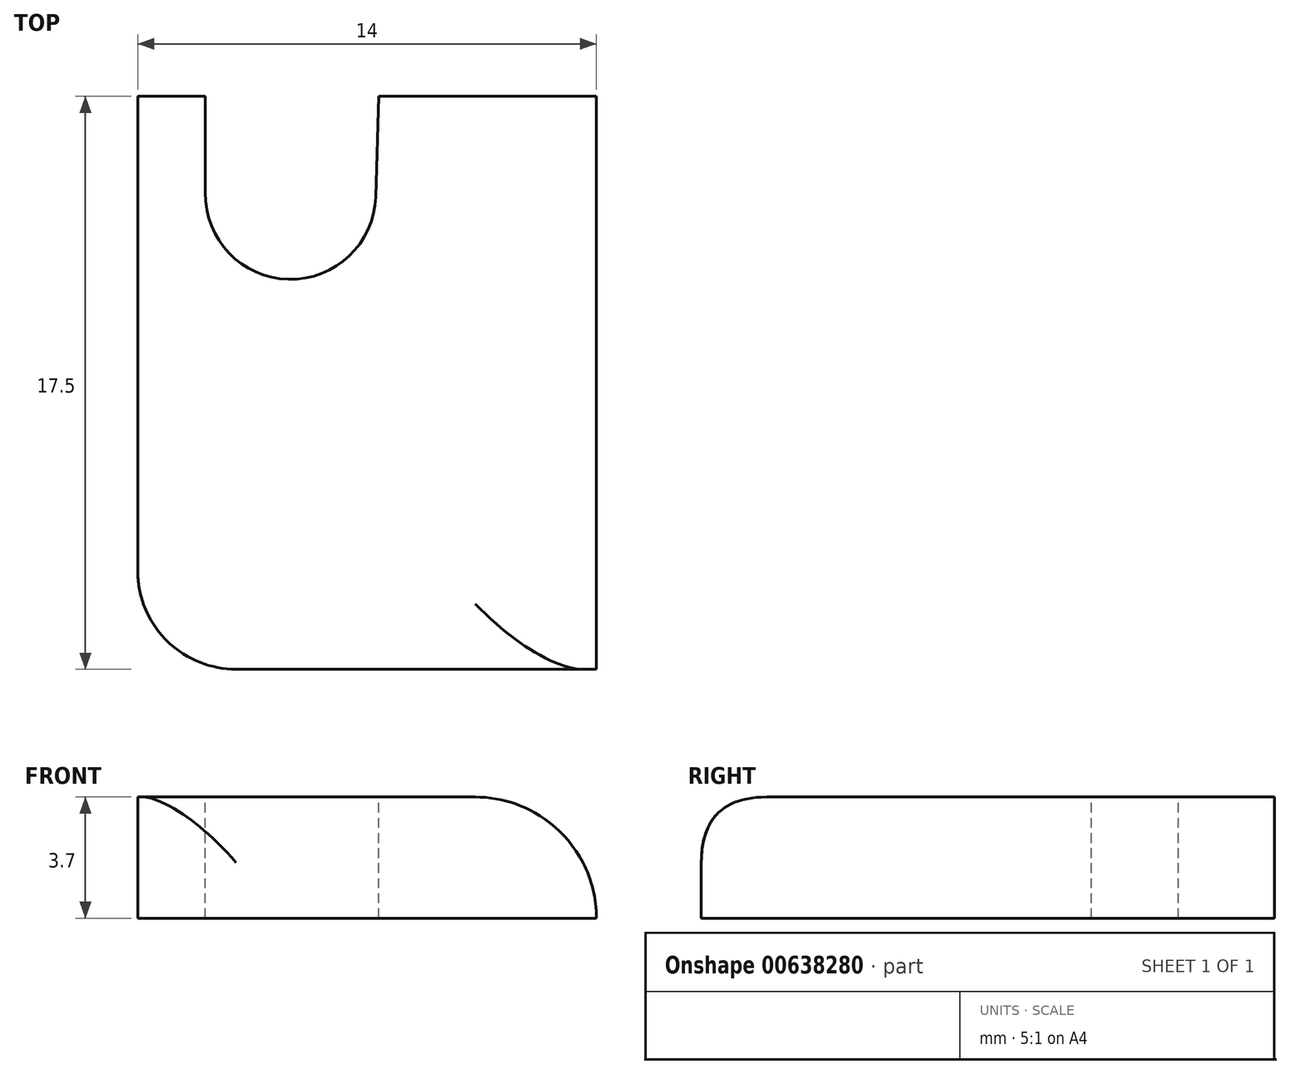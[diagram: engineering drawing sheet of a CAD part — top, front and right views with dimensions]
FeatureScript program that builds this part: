
annotation { "Feature Type Name" : "Feature", "Feature Type Description" : "" }
export const myFeature = defineFeature(function(context is Context, id is Id, definition is map)
    precondition{}
    {
        {
            var Q0;
            Q0=qCreatedBy(makeId("Top.planeOp"),FACE);
            var sketch = newSketch(context, id + "F0", { "sketchPlane" : qUnion([Q0])});
            skLineSegment(sketch, "E0.bottom", {"start": v(-7.41, 12.17) * mm, "end": v(6.59, 12.17) * mm});
            skLineSegment(sketch, "E0.top", {"start": v(-7.41, -5.33) * mm, "end": v(6.59, -5.33) * mm});
            skLineSegment(sketch, "E0.left", {"start": v(-7.41, 12.17) * mm, "end": v(-7.41, -5.33) * mm});
            skLineSegment(sketch, "E0.right", {"start": v(6.59, 12.17) * mm, "end": v(6.59, -5.33) * mm});
            skSolve(sketch);
        }
        {
            var Q0;
            Q0 = qSketchRegion(id + "F0", true);
            extrude(context, id + "F1", {"entities" : qUnion([Q0]), "depth" : 3.7 * mm, "offsetDistance" : 25 * mm});
        }
        {
            var Q0;
            Q0=makeQuery(id+"F1.opExtrude","CAP_FACE",FACE,{"disambiguationData":[OSD([sQuery(id+"F0.wireOp",EDGE,"E0.bottom"),sQuery(id+"F0.wireOp",EDGE,"E0.top"),sQuery(id+"F0.wireOp",EDGE,"E0.left"),sQuery(id+"F0.wireOp",EDGE,"E0.right")])],"isStart":false});
            var sketch = newSketch(context, id + "F2", { "sketchPlane" : qUnion([Q0])});
            skArc(sketch, "E1", {"start": v(-5.35, 9.23) * mm, "mid": v(-2.8, 6.58) * mm, "end": v(-0.15, 9.1) * mm});
            skLineSegment(sketch, "E2", {"start": v(-0.15, 9.1) * mm, "end": v(-0.06, 12.17) * mm});
            skLineSegment(sketch, "E3", {"start": v(-5.35, 9.13) * mm, "end": v(-5.35, 12.17) * mm});
            skSolve(sketch);
        }
        {
            var Q0;
            Q0 = qSketchRegion(id + "F2", true);
            var Q1;
            {var subQ0=sQuery(id+"F2.wireOp",EDGE,"E2");Q1=makeQuery(id+"F2.imprint","IMPRINT",FACE,{"disambiguationData":[TD([[makeQuery(id+"F2.imprint","IMPRINT",EDGE,{"derivedFrom":subQ0}),1.0]])]});}
            extrude(context, id + "F3", {"entities" : qUnion([Q0, Q1]), "operationType" : NewBodyOperationType.REMOVE, "oppositeDirection" : true, "depth" : 5.4 * mm, "offsetDistance" : 25 * mm});
        }
        {
            var Q0;
            Q0=makeQuery(id+"F1.opExtrude","CAP_EDGE",EDGE,{"disambiguationData":[OSD([sQuery(id+"F0.wireOp",EDGE,"E0.right")])],"isStart":false});
            fillet(context, id + "F4", {"entities" : qUnion([Q0]), "radius" : 3.7 * mm, "tangentPropagation" : true, "allowEdgeOverflow" : false});
        }
        {
            var Q0;
            Q0=makeQuery(id+"F1.opExtrude","SWEPT_EDGE",EDGE,{"disambiguationData":[OSD([sQuery(id+"F0.wireOp",EDGE,"E0.top"),sQuery(id+"F0.wireOp",EDGE,"E0.left")])]});
            fillet(context, id + "F5", {"entities" : qUnion([Q0]), "radius" : 3 * mm, "tangentPropagation" : true, "allowEdgeOverflow" : false});
        }
        {
            var Q0;
            Q0=makeQuery(id+"F1.opExtrude","CAP_EDGE",EDGE,{"disambiguationData":[OSD([sQuery(id+"F0.wireOp",EDGE,"E0.top")])],"isStart":false});
            fillet(context, id + "F6", {"entities" : qUnion([Q0]), "radius" : 2 * mm, "rho" : 0.5, "crossSection" : FilletCrossSection.CONIC, "allowEdgeOverflow" : false});
        }
    });
